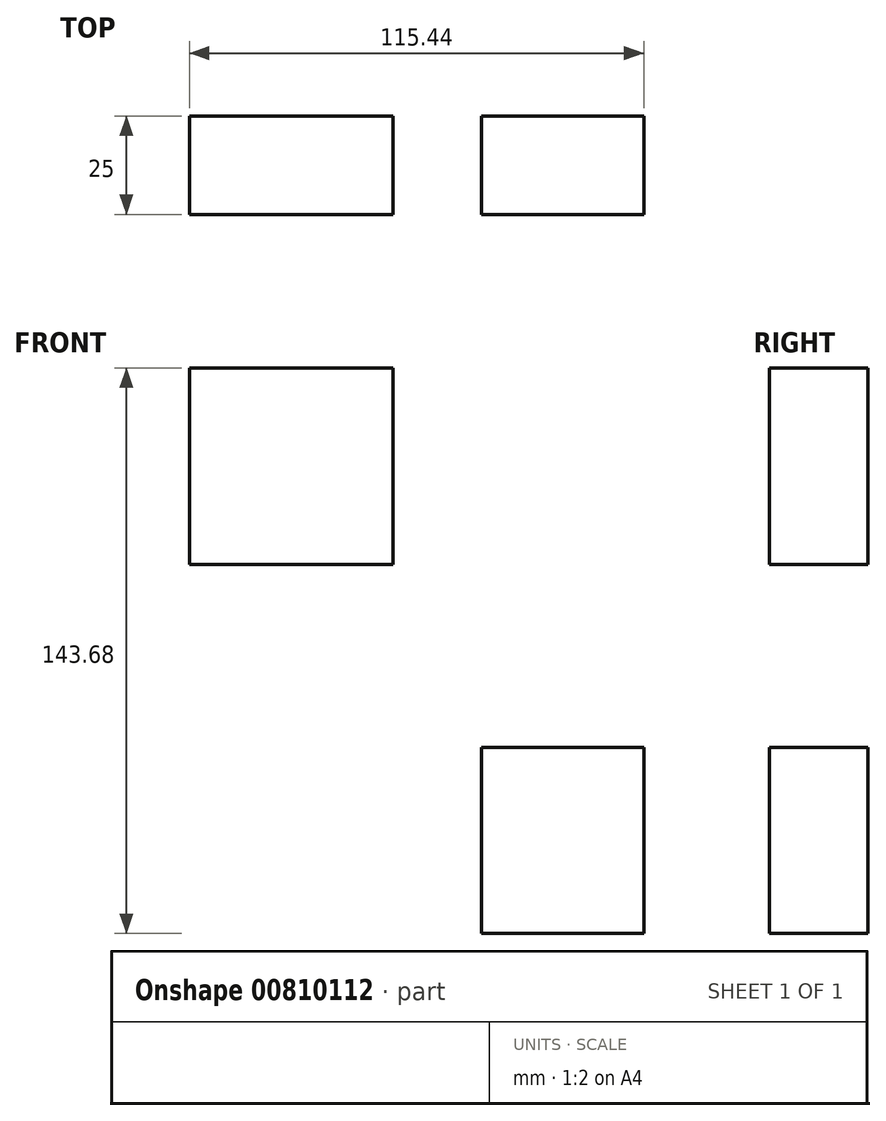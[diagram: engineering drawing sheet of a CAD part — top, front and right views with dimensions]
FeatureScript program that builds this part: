
annotation { "Feature Type Name" : "Feature", "Feature Type Description" : "" }
export const myFeature = defineFeature(function(context is Context, id is Id, definition is map)
    precondition{}
    {
        {
            var Q0;
            Q0=qCreatedBy(makeId("Front.planeOp"),FACE);
            var sketch = newSketch(context, id + "F0", { "sketchPlane" : qUnion([Q0])});
            skLineSegment(sketch, "E0.bottom", {"start": v(-32.5, 87.38) * mm, "end": v(19.18, 87.38) * mm});
            skLineSegment(sketch, "E0.top", {"start": v(-32.5, 37.47) * mm, "end": v(19.18, 37.47) * mm});
            skLineSegment(sketch, "E0.left", {"start": v(-32.5, 87.38) * mm, "end": v(-32.5, 37.47) * mm});
            skLineSegment(sketch, "E0.right", {"start": v(19.18, 87.38) * mm, "end": v(19.18, 37.47) * mm});
            skLineSegment(sketch, "E1.bottom", {"start": v(41.74, -9.06) * mm, "end": v(82.94, -9.06) * mm});
            skLineSegment(sketch, "E1.top", {"start": v(41.74, -56.3) * mm, "end": v(82.94, -56.3) * mm});
            skLineSegment(sketch, "E1.left", {"start": v(41.74, -9.06) * mm, "end": v(41.74, -56.3) * mm});
            skLineSegment(sketch, "E1.right", {"start": v(82.94, -9.06) * mm, "end": v(82.94, -56.3) * mm});
            skSolve(sketch);
        }
        {
            var Q0;
            Q0 = qSketchRegion(id + "F0", true);
            extrude(context, id + "F1", {"entities" : qUnion([Q0]), "depth" : 25 * mm, "offsetDistance" : 25 * mm});
        }
    });
